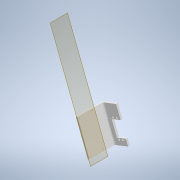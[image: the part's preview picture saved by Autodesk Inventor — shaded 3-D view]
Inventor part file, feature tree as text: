
AUTODESK INVENTOR PART (.ipt)
format: ipt  version: 2021 (Build 250183000, 183)  size: 159,232 bytes
history: native  units: mm
features: sketch x5, other x3, plane x2
ambient origin geometry x8: Origin, YZ Plane, XZ Plane, XY Plane, X Axis, Y Axis, Z Axis, Center Point
bodies: Solid1 (feature_tree)
feature tree (10):
  other  "servo_mount.ipt"
  other  "Solid1::servo_mount.ipt"
  other  "TaggingFeature1"
  sketch  "Sketch1"  dims[d0=10.0mm]
  sketch  "Sketch2"
  sketch  "Sketch3"
  sketch  "Sketch4"
  sketch  "Sketch5"
  plane  "Work Plane1"
  plane  "Work Plane2"
